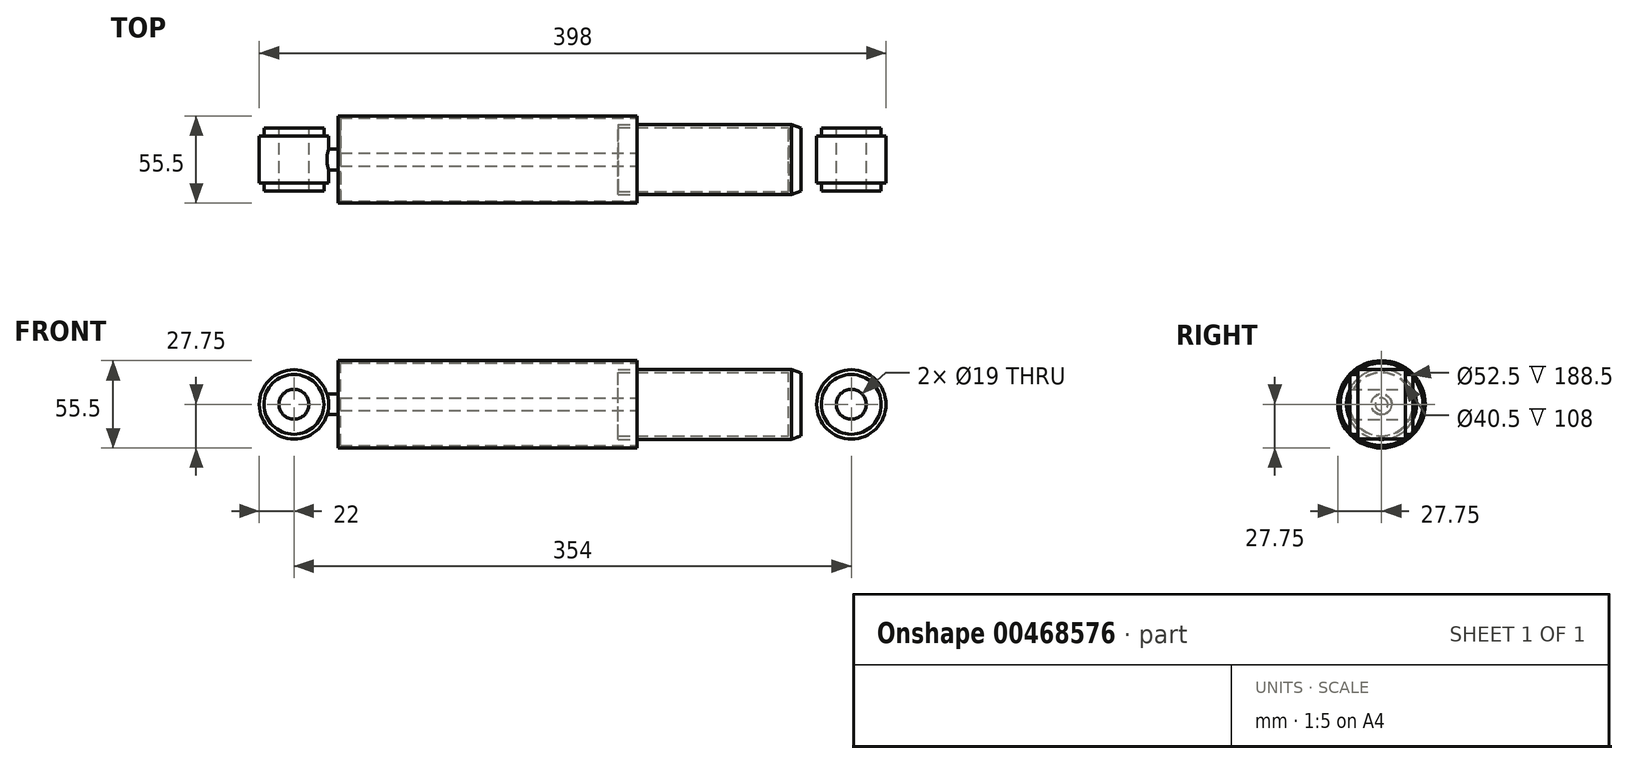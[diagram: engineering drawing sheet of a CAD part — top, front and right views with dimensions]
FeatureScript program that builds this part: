
annotation { "Feature Type Name" : "Feature", "Feature Type Description" : "" }
export const myFeature = defineFeature(function(context is Context, id is Id, definition is map)
    precondition{}
    {
        {
            var Q0;
            Q0=qCreatedBy(makeId("Front.planeOp"),FACE);
            var sketch = newSketch(context, id + "F0", { "sketchPlane" : qUnion([Q0])});
            skLineSegment(sketch, "E0", {"start": v(0, 0) * mm, "end": v(496, 0) * mm, "construction": true});
            skCircle(sketch, "E1", {"center": v(0, 0) * mm, "radius": 22 * mm});
            skPoint(sketch, "E2", {"position": v(218, 0) * mm});
            skLineSegment(sketch, "E3", {"start": v(218, 0) * mm, "end": v(218, 27.75) * mm});
            skLineSegment(sketch, "E4", {"start": v(218, 27.75) * mm, "end": v(28, 27.75) * mm});
            skLineSegment(sketch, "E5", {"start": v(28, 27.75) * mm, "end": v(28, 0) * mm});
            skLineSegment(sketch, "E6", {"start": v(28, 0) * mm, "end": v(29.5, 0) * mm});
            skLineSegment(sketch, "E7", {"start": v(29.5, 0) * mm, "end": v(29.5, 26.25) * mm});
            skLineSegment(sketch, "E8", {"start": v(29.5, 26.25) * mm, "end": v(218, 26.25) * mm});
            skPoint(sketch, "E9", {"position": v(316, 0) * mm});
            skLineSegment(sketch, "E10", {"start": v(316, 0) * mm, "end": v(316, 22.25) * mm});
            skLineSegment(sketch, "E11", {"start": v(316, 22.25) * mm, "end": v(206, 22.25) * mm});
            skLineSegment(sketch, "E12", {"start": v(206, 22.25) * mm, "end": v(206, 20.25) * mm});
            skLineSegment(sketch, "E13", {"start": v(206, 20.25) * mm, "end": v(314, 20.25) * mm});
            skLineSegment(sketch, "E14", {"start": v(314, 20.25) * mm, "end": v(314, 0) * mm});
            skLineSegment(sketch, "E15", {"start": v(314, 0) * mm, "end": v(316, 0) * mm});
            skLineSegment(sketch, "E16", {"start": v(29.5, 4) * mm, "end": v(314, 4) * mm});
            skLineSegment(sketch, "E17", {"start": v(314, 4) * mm, "end": v(314, 0) * mm});
            skLineSegment(sketch, "E18", {"start": v(314, 0) * mm, "end": v(29.5, 0) * mm});
            skLineSegment(sketch, "E19", {"start": v(28, 0) * mm, "end": v(22, 0) * mm});
            skPoint(sketch, "E20", {"position": v(21, 0) * mm});
            skLineSegment(sketch, "E21", {"start": v(21, 0) * mm, "end": v(21, 6.56) * mm});
            skLineSegment(sketch, "E22", {"start": v(21, 6.56) * mm, "end": v(28, 6.56) * mm});
            skCircle(sketch, "E23", {"center": v(496, 0) * mm, "radius": 22 * mm});
            skLineSegment(sketch, "E24", {"start": v(316, 0) * mm, "end": v(322, 0) * mm});
            skLineSegment(sketch, "E25", {"start": v(322, 0) * mm, "end": v(322, 20) * mm});
            skLineSegment(sketch, "E26", {"start": v(322, 20) * mm, "end": v(316, 22.25) * mm});
            skLineSegment(sketch, "E27", {"start": v(322, 0) * mm, "end": v(474, 0) * mm});
            skLineSegment(sketch, "E28", {"start": v(333, 0) * mm, "end": v(322, 0) * mm});
            skLineSegment(sketch, "E29", {"start": v(333, 0) * mm, "end": v(333, 8) * mm});
            skLineSegment(sketch, "E30", {"start": v(333, 8) * mm, "end": v(322, 8) * mm});
            skSolve(sketch);
        }
        {
            var Q0;
            {var subQ3=sQuery(id+"F0.wireOp",EDGE,"E4");Q0=makeQuery(id+"F0.imprint","IMPRINT",FACE,{"disambiguationData":[TD([[makeQuery(id+"F0.imprint","IMPRINT",EDGE,{"derivedFrom":subQ3}),1.0]])]});}
            var Q1;
            {var subQ0=sQuery(id+"F0.wireOp",EDGE,"E19");Q1=makeQuery(id+"F0.imprint","IMPRINT",FACE,{"disambiguationData":[TD([[makeQuery(id+"F0.imprint","IMPRINT",EDGE,{"derivedFrom":subQ0}),-1.0]])]});}
            var Q2;
            {var subQ0=sQuery(id+"F0.wireOp",EDGE,"E18");var subQ1=sQuery(id+"F0.wireOp",EDGE,"E3");var subQ2=makeQuery(id+"F0.imprint","INTERSECT",VERTEX,{"derivedFrom":[subQ1,subQ0]});Q2=makeQuery(id+"F0.imprint","IMPRINT",FACE,{"disambiguationData":[TD([[makeQuery(id+"F0.imprint","IMPRINT",EDGE,{"disambiguationData":[TD([[subQ2,-1.0]])],"derivedFrom":subQ1}),1.0]])]});}
            var Q3;
            {var subQ1=sQuery(id+"F0.wireOp",EDGE,"E10");Q3=makeQuery(id+"F0.imprint","IMPRINT",FACE,{"disambiguationData":[TD([[makeQuery(id+"F0.imprint","IMPRINT",EDGE,{"derivedFrom":subQ1}),1.0]])]});}
            var Q4;
            {var subQ5=sQuery(id+"F0.wireOp",EDGE,"E12");Q4=makeQuery(id+"F0.imprint","IMPRINT",FACE,{"disambiguationData":[TD([[makeQuery(id+"F0.imprint","IMPRINT",EDGE,{"derivedFrom":subQ5}),1.0]])]});}
            var Q5;
            Q5=makeQuery(id+"F0.imprint","IMPRINT",FACE,{"disambiguationData":[TD([[makeQuery(id+"F0.imprint","IMPRINT",EDGE,{"derivedFrom":sQuery(id+"F0.wireOp",EDGE,"E10")}),-1.0]])]});
            var Q6;
            {var subQ0=sQuery(id+"F0.wireOp",EDGE,"E28");Q6=makeQuery(id+"F0.imprint","IMPRINT",FACE,{"disambiguationData":[TD([[makeQuery(id+"F0.imprint","IMPRINT",EDGE,{"derivedFrom":subQ0}),-1.0]])]});}
            var Q7;
            {var subQ5=sQuery(id+"F0.wireOp",EDGE,"E17");Q7=makeQuery(id+"F0.imprint","IMPRINT",FACE,{"disambiguationData":[TD([[makeQuery(id+"F0.imprint","IMPRINT",EDGE,{"derivedFrom":subQ5}),-1.0]])]});}
            var Q8;
            Q8=sQuery(id+"F0.wireOp",EDGE,"E18");
            revolve(context, id + "F1", {"surfaceOperationType" : NewSurfaceOperationType.NEW, "entities" : qUnion([Q0, Q1, Q2, Q3, Q4, Q5, Q6, Q7]), "axis" : qUnion([Q8]), "revolveType" : RevolveType.FULL});
        }
        {
            var Q0;
            Q0=qCreatedBy(makeId("Front.planeOp"),FACE);
            var sketch = newSketch(context, id + "F2", { "sketchPlane" : qUnion([Q0])});
            skCircle(sketch, "E31", {"center": v(0, 0) * mm, "radius": 22 * mm});
            skCircle(sketch, "E32", {"center": v(0, 0) * mm, "radius": 19 * mm});
            skLineSegment(sketch, "E33.0", {"start": v(333, 8) * mm, "end": v(333, -8) * mm});
            skPoint(sketch, "E34", {"position": v(354, 0) * mm});
            skPoint(sketch, "E34.positionSnap0", {"position": v(333, 0) * mm});
            skCircle(sketch, "E35", {"center": v(354, 0) * mm, "radius": 22 * mm});
            skCircle(sketch, "E36", {"center": v(354, 0) * mm, "radius": 19 * mm});
            skSolve(sketch);
        }
        {
            var Q0;
            Q0=qSketchRegion(id+"F2",true);
            extrude(context, id + "F3", {"entities" : qUnion([Q0]), "operationType" : NewBodyOperationType.ADD, "depth" : 30 * mm, "offsetDistance" : 25 * mm, "symmetric" : true});
        }
        {
            var Q0;
            Q0=qCreatedBy(makeId("Front.planeOp"),FACE);
            var sketch = newSketch(context, id + "F4", { "sketchPlane" : qUnion([Q0])});
            skCircle(sketch, "E37.0", {"center": v(0, 0) * mm, "radius": 19 * mm});
            skCircle(sketch, "E38", {"center": v(0, 0) * mm, "radius": 9.5 * mm});
            skCircle(sketch, "E39.0", {"center": v(354, 0) * mm, "radius": 19 * mm});
            skCircle(sketch, "E40", {"center": v(354, 0) * mm, "radius": 9.5 * mm});
            skSolve(sketch);
        }
        {
            var Q0;
            Q0 = qSketchRegion(id + "F4", true);
            extrude(context, id + "F5", {"entities" : qUnion([Q0]), "operationType" : NewBodyOperationType.ADD, "depth" : 40 * mm, "offsetDistance" : 25 * mm, "symmetric" : true});
        }
    });
